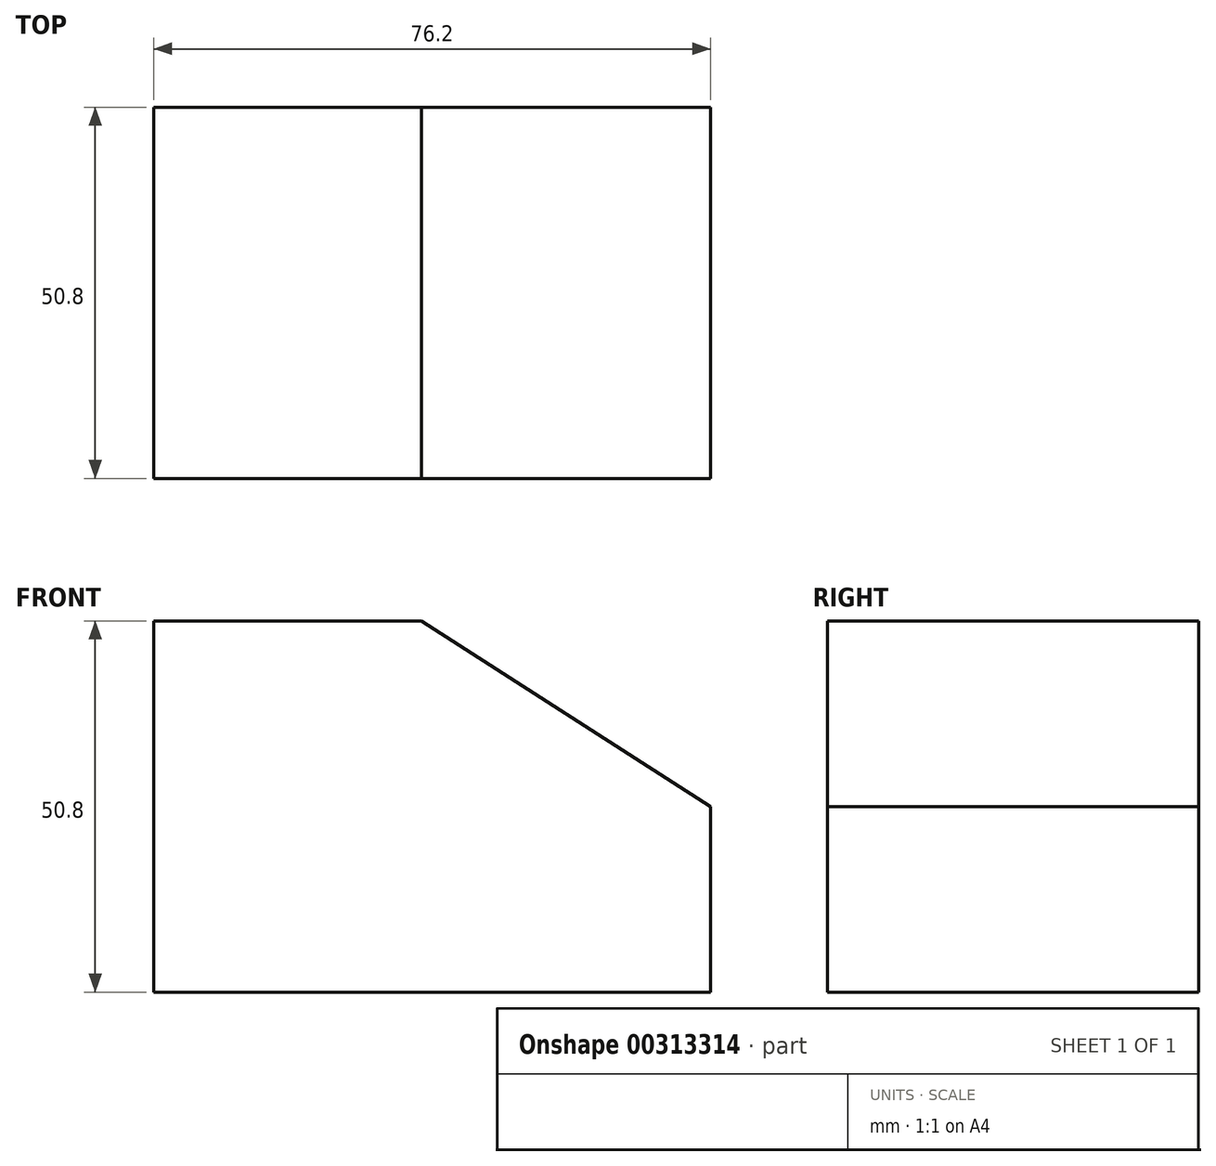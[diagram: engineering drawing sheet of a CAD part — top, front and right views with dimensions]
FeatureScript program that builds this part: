
annotation { "Feature Type Name" : "Feature", "Feature Type Description" : "" }
export const myFeature = defineFeature(function(context is Context, id is Id, definition is map)
    precondition{}
    {
        {
            var Q0;
            Q0=qCreatedBy(makeId("Front.planeOp"),FACE);
            var sketch = newSketch(context, id + "F0", { "sketchPlane" : qUnion([Q0])});
            skLineSegment(sketch, "E0", {"start": v(-30.98, -28.94) * mm, "end": v(45.22, -28.94) * mm});
            skLineSegment(sketch, "E1", {"start": v(-30.98, -28.94) * mm, "end": v(-30.98, 21.86) * mm});
            skLineSegment(sketch, "E2", {"start": v(45.22, -28.94) * mm, "end": v(45.22, -3.54) * mm});
            skLineSegment(sketch, "E3", {"start": v(-30.98, 21.86) * mm, "end": v(5.66, 21.86) * mm});
            skLineSegment(sketch, "E4", {"start": v(5.66, 21.86) * mm, "end": v(45.22, -3.54) * mm});
            skSolve(sketch);
        }
        {
            var Q0;
            Q0=makeQuery(id+"F0.imprint","IMPRINT",FACE,{"disambiguationData":[TD([[makeQuery(id+"F0.imprint","IMPRINT",EDGE,{"derivedFrom":sQuery(id+"F0.wireOp",EDGE,"E0")}),1.0]])]});
            extrude(context, id + "F1", {"entities" : qUnion([Q0]), "depth" : 50.8 * mm});
        }
    });
